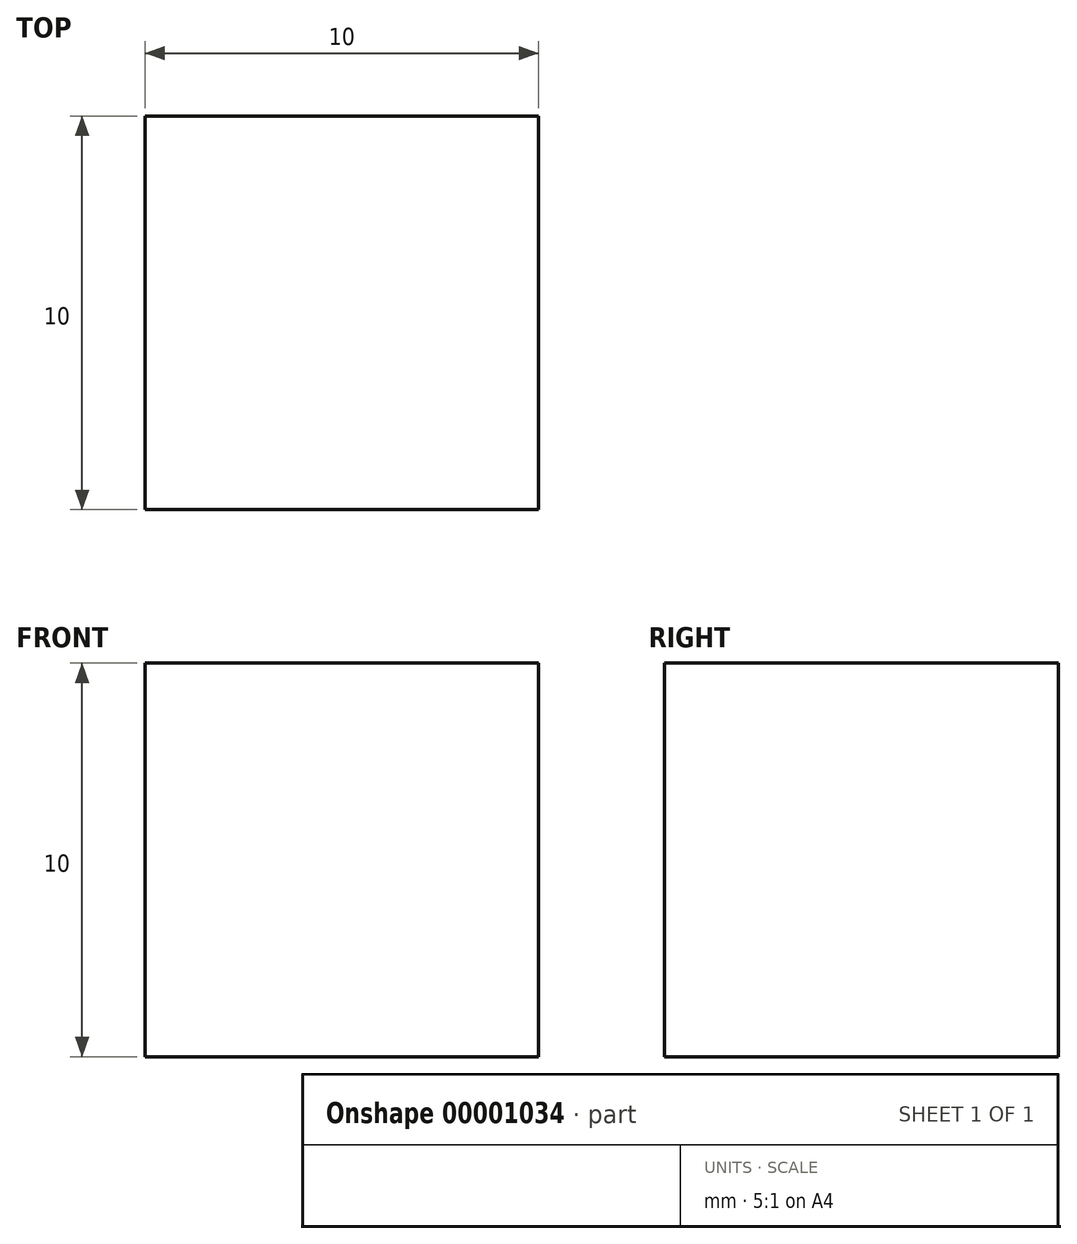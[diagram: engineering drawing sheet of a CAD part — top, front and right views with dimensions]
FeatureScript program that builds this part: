
annotation { "Feature Type Name" : "Feature", "Feature Type Description" : "" }
export const myFeature = defineFeature(function(context is Context, id is Id, definition is map)
    precondition{}
    {
        {
            var Q0;
            Q0=qCreatedBy(makeId("Front.planeOp"),FACE);
            var sketch = newSketch(context, id + "F0", { "sketchPlane" : qUnion([Q0])});
            skLineSegment(sketch, "E0.bottom", {"start": v(-5, 5) * mm, "end": v(5, 5) * mm});
            skLineSegment(sketch, "E0.top", {"start": v(-5, -5) * mm, "end": v(5, -5) * mm});
            skLineSegment(sketch, "E0.left", {"start": v(-5, 5) * mm, "end": v(-5, -5) * mm});
            skLineSegment(sketch, "E0.right", {"start": v(5, 5) * mm, "end": v(5, -5) * mm});
            skSolve(sketch);
        }
        {
            var Q0;
            Q0=makeQuery(id+"F0.imprint","IMPRINT",FACE,{"disambiguationData":[TD([[makeQuery(id+"F0.imprint","IMPRINT",EDGE,{"derivedFrom":sQuery(id+"F0.wireOp",EDGE,"E0.bottom")}),-1.0]])]});
            extrude(context, id + "F1", {"entities" : qUnion([Q0]), "depth" : 10 * mm});
        }
    });
